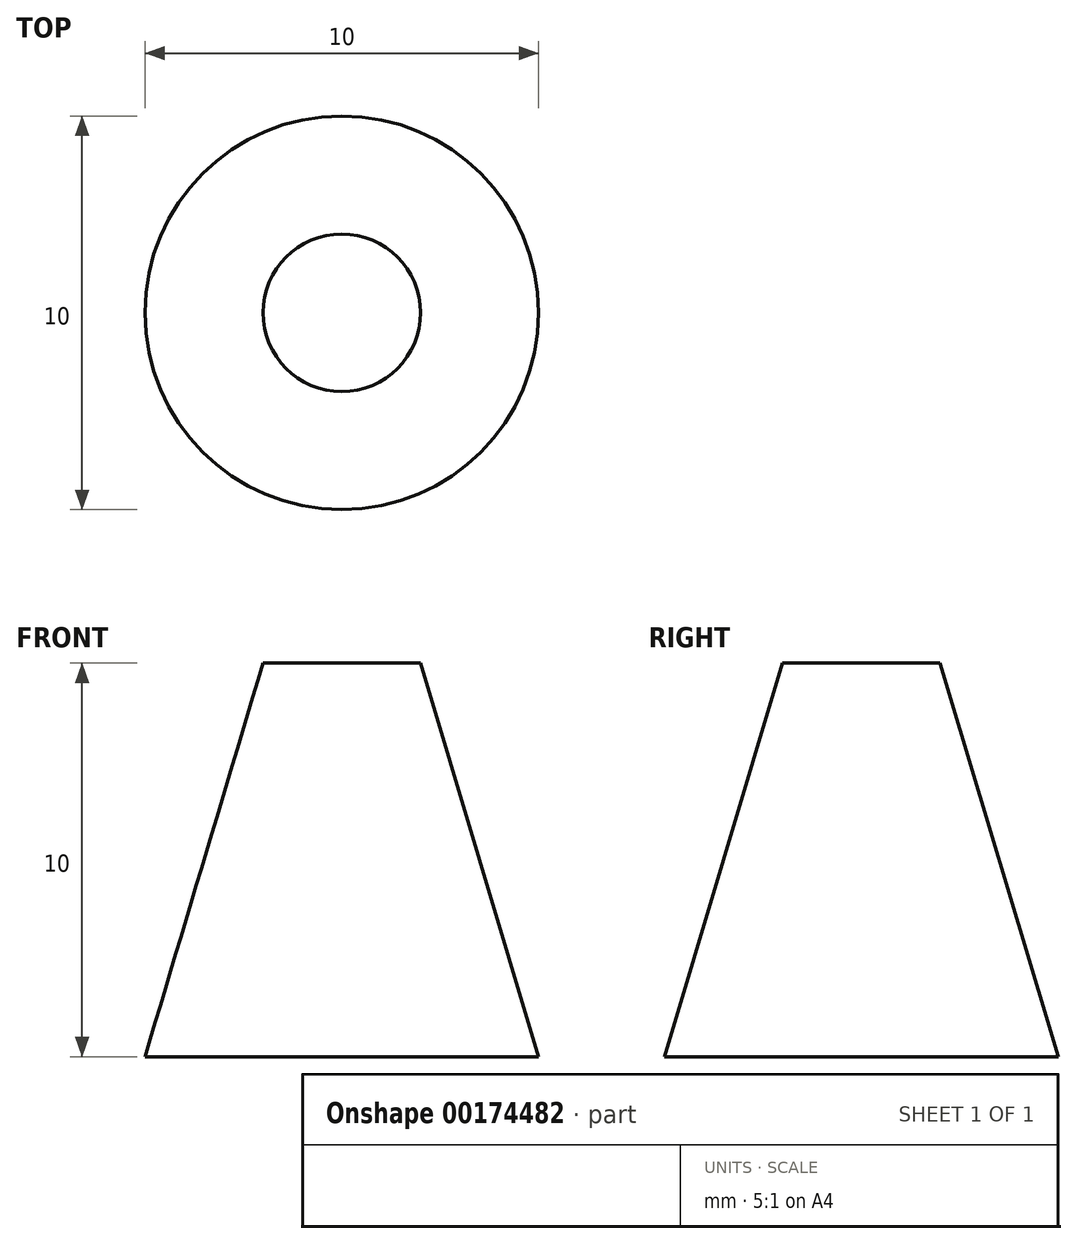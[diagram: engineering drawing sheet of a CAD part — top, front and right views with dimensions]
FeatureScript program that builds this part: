
annotation { "Feature Type Name" : "Feature", "Feature Type Description" : "" }
export const myFeature = defineFeature(function(context is Context, id is Id, definition is map)
    precondition{}
    {
        {
            var Q0;
            Q0=qCreatedBy(makeId("Front.planeOp"),FACE);
            var sketch = newSketch(context, id + "F0", { "sketchPlane" : qUnion([Q0])});
            skLineSegment(sketch, "E0", {"start": v(0, 0) * mm, "end": v(0, 19.35) * mm, "construction": true});
            skLineSegment(sketch, "E1", {"start": v(0, 0) * mm, "end": v(-5, 0) * mm});
            skLineSegment(sketch, "E2", {"start": v(-5, 0) * mm, "end": v(-2, 10) * mm});
            skLineSegment(sketch, "E3", {"start": v(-2, 10) * mm, "end": v(0, 10) * mm});
            skLineSegment(sketch, "E4", {"start": v(0, 10) * mm, "end": v(0, 0) * mm});
            skSolve(sketch);
        }
        {
            var Q0;
            Q0 = qSketchRegion(id + "F0", true);
            var Q1;
            Q1=sQuery(id+"F0.wireOp",EDGE,"E0");
            revolve(context, id + "F1", {"entities" : qUnion([Q0]), "axis" : qUnion([Q1]), "revolveType" : RevolveType.FULL});
        }
    });
